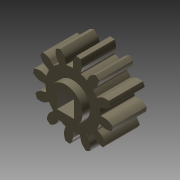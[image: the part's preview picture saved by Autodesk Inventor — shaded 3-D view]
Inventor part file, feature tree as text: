
AUTODESK INVENTOR PART (.ipt)
format: ipt  version: 2013 (Build 170138000, 138)  size: 480,768 bytes
history: native  units: mm (DEFAULTED — no unit token found)
features: imported_body x1, sketch x1, other x1, extrude x1
ambient origin geometry x8: Origin, YZ Plane, XZ Plane, XY Plane, X Axis, Y Axis, Z Axis, Center Point
bodies: Solid1 (feature_tree)
feature tree (4):
  imported_body  "Base1"
  sketch  "Sketch2"  dims[d1=6.35mm d3=25.4mm d4=0.0mm d5=0.0mm d6=0.0mm]
  other  "Srf1"
  extrude  "ExtrusionSrf1"  Depth=25.4mm TaperAngle=0.0deg
